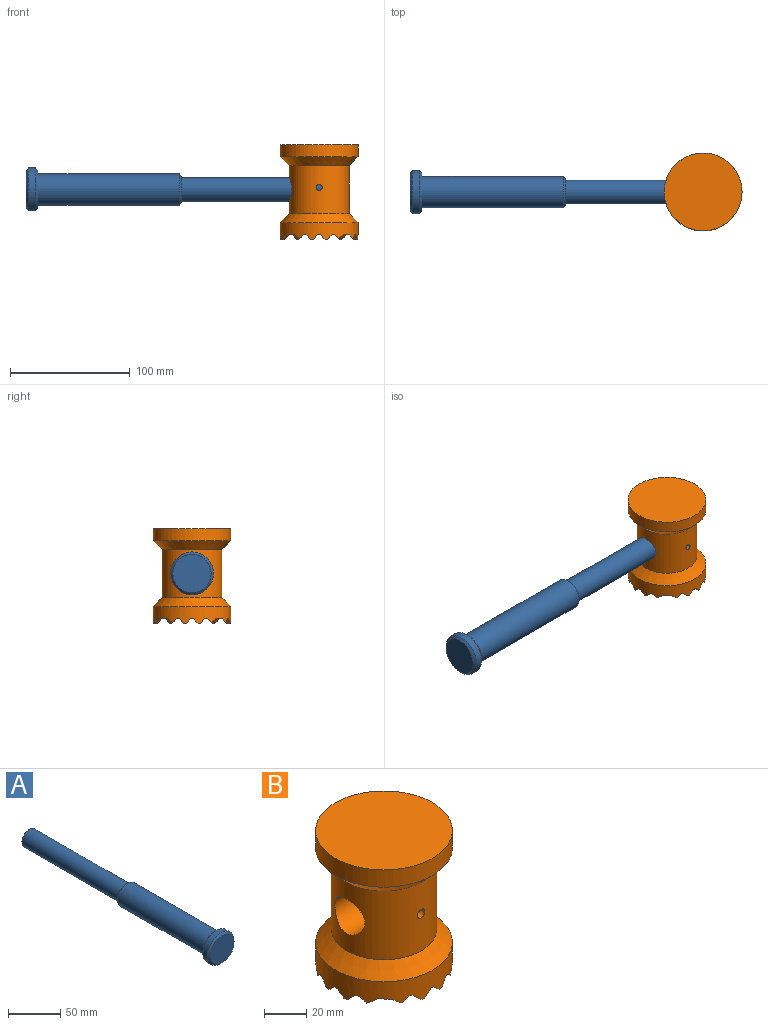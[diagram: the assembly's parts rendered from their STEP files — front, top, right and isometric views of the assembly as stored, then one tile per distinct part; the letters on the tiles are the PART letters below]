
ASSEMBLY  parts=2 mates=1
PART A: 10 faces, bbox 36x260x36 mm
  f0: cylinder r=10mm len=130mm, axis (0,1,0), area 8168.1mm2, adj f1,f3
  f1: plane 20x20mm, normal (0,1,0), area 314.2mm2, adj f0
  f2: cylinder r=13mm len=118mm, axis (0,1,0), area 9638.4mm2, adj f6,f9
  f3: plane 22x22mm, normal (0,1,0), area 66mm2, adj f0,f9
  f4: cylinder r=18mm len=36mm, axis (0,1,0), area 678.6mm2, adj f7,f8
  f5: plane 32x32mm, normal (0,-1,0), area 804.2mm2, adj f8
  f6: plane 32x32mm, normal (0,1,0), area 273.3mm2, adj f2,f7
  f7: cone r=18mm half-angle=45deg, axis (0,-1,0), area 302.1mm2, adj f4,f6
  f8: cone r=16mm half-angle=45deg, axis (0,1,0), area 302.1mm2, adj f4,f5
  f9: cone r=13mm half-angle=45deg, axis (0,-1,0), area 213.3mm2, adj f2,f3
PART B: 137 faces, bbox 65x65x79 mm
  f0: cylinder r=25mm len=50mm, axis (0,0,1), area 5923.4mm2, adj f1,f29,f30,f135,f136
  f1: cylinder r=10mm len=40mm, axis (1,0,0), area 2408.1mm2, adj f0,f134,f135,f136
  f2: plane 2x2mm, normal (0,0,-1), area 4mm2, adj f25,f49,f125,f126
  f3: plane 2x2mm, normal (0,0,-1), area 4mm2, adj f25,f49,f105,f124
  f4: plane 2x2mm, normal (0,0,-1), area 4mm2, adj f25,f49,f99,f104
  f5: plane 2x2mm, normal (0,0,-1), area 4mm2, adj f25,f49,f83,f98
  f6: plane 3.01x2mm, normal (0,0,-1), area 5.7mm2, adj f22,f50,f51,f131
  f7: plane 2x2mm, normal (0,0,-1), area 4mm2, adj f50,f51,f123,f130
  f8: plane 2x2mm, normal (0,0,-1), area 4mm2, adj f50,f51,f107,f122
  f9: plane 2x2mm, normal (0,0,-1), area 4mm2, adj f50,f51,f97,f106
  f10: plane 2x2mm, normal (0,0,-1), area 4mm2, adj f50,f51,f85,f96
  f11: plane 3.01x2mm, normal (0,0,-1), area 5.7mm2, adj f22,f52,f53,f132
  f12: plane 2x2mm, normal (0,0,-1), area 4mm2, adj f52,f53,f119,f129
  f13: plane 2x2mm, normal (0,0,-1), area 4mm2, adj f52,f53,f109,f118
  f14: plane 2x2mm, normal (0,0,-1), area 4mm2, adj f52,f53,f95,f108
  f15: plane 2x2mm, normal (0,0,-1), area 4mm2, adj f52,f53,f87,f94
  f16: plane 2x2mm, normal (0,0,-1), area 4mm2, adj f26,f54,f117,f128
  f17: plane 2x2mm, normal (0,0,-1), area 4mm2, adj f26,f54,f111,f116
  f18: plane 2x2mm, normal (0,0,-1), area 4mm2, adj f26,f54,f93,f110
  f19: plane 2x2mm, normal (0,0,-1), area 4mm2, adj f26,f54,f89,f92
  f20: plane 3.1x2mm, normal (0,0,-1), area 5.8mm2, adj f22,f55,f113,f114
  f21: plane 3.13x2mm, normal (0,0,-1), area 5.9mm2, adj f22,f55,f91,f112
  f22: cylinder r=32.5mm len=65mm, axis (0,0,1), area 2364.1mm2, adj f6,f11,f20,f21,f23,f24,f25,f26
  f23: plane 3.1x2mm, normal (0,0,-1), area 5.8mm2, adj f22,f48,f103,f120
  f24: plane 3.13x2mm, normal (0,0,-1), area 5.9mm2, adj f22,f48,f101,f102
  f25: plane 46.43x4mm, normal (-0.71,0,-0.71), area 138.4mm2, adj f2,f3,f4,f5,f22,f45,f74,f75
  f26: plane 46.43x4mm, normal (0.71,0,-0.71), area 138.4mm2, adj f16,f17,f18,f19,f22,f35,f59,f60
  f27: plane 3.21x2mm, normal (0,0,-1), area 6.1mm2, adj f22,f50,f51,f84
  f28: plane 3.21x2mm, normal (0,0,-1), area 6.1mm2, adj f22,f52,f53,f86
  f29: cone r=25mm half-angle=45deg, axis (0,0,-1), area 1916mm2, adj f0,f22
  f30: cone r=32.5mm half-angle=45deg, axis (0,0,1), area 1916mm2, adj f0,f31
  f31: cylinder r=32.5mm len=65mm, axis (0,0,1), area 2042mm2, adj f30,f32
  f32: plane 65x65mm, normal (0,0,1), area 3318.3mm2, adj f31
  f33: plane 41.53x0.01mm, normal (-1,0,0), area 0.6mm2, adj f22,f34,f55
  f34: plane 45.92x2mm, normal (0,0,-1), area 87.6mm2, adj f22,f33,f35
  f35: plane 45.92x0.01mm, normal (1,0,0), area 0.7mm2, adj f22,f26,f34
  f36: plane 59.57x0.01mm, normal (-1,0,0), area 0.9mm2, adj f22,f37,f54
  f37: plane 61.16x2mm, normal (0,0,-1), area 120.8mm2, adj f22,f36,f38
  f38: plane 61.16x0.01mm, normal (1,0,0), area 0.9mm2, adj f22,f37,f53
  f39: plane 64.97x0.01mm, normal (-1,0,0), area 1mm2, adj f22,f40,f52
  f40: plane 65x2mm, normal (0,0,-1), area 130mm2, adj f22,f39,f41
  f41: plane 64.97x0.01mm, normal (1,0,0), area 1mm2, adj f22,f40,f51
  f42: plane 61.16x0.01mm, normal (-1,0,0), area 0.9mm2, adj f22,f43,f50
  f43: plane 61.16x2mm, normal (0,0,-1), area 120.8mm2, adj f22,f42,f44
  f44: plane 59.57x0.01mm, normal (1,0,0), area 0.9mm2, adj f22,f43,f49
  f45: plane 45.92x0.01mm, normal (-1,0,0), area 0.7mm2, adj f22,f25,f46
  f46: plane 45.92x2mm, normal (0,0,-1), area 87.6mm2, adj f22,f45,f47
  f47: plane 41.53x0.01mm, normal (1,0,0), area 0.6mm2, adj f22,f46,f48
  f48: plane 41.53x4mm, normal (0.71,0,-0.71), area 106.6mm2, adj f22,f23,f24,f47,f79,f80,f81,f100
  f49: plane 59.57x4mm, normal (0.71,0,-0.71), area 161.7mm2, adj f2,f3,f4,f5,f22,f44,f74,f75
  f50: plane 63.47x4mm, normal (-0.71,0,-0.71), area 187.4mm2, adj f6,f7,f8,f9,f10,f22,f27,f42
  f51: plane 64.98x4.01mm, normal (0.71,0,-0.71), area 200.3mm2, adj f6,f7,f8,f9,f10,f22,f27,f41
  f52: plane 64.98x4.01mm, normal (-0.71,0,-0.71), area 200.3mm2, adj f11,f12,f13,f14,f15,f22,f28,f39
  f53: plane 63.47x4mm, normal (0.71,0,-0.71), area 187.4mm2, adj f11,f12,f13,f14,f15,f22,f28,f38
  f54: plane 59.57x4mm, normal (-0.71,0,-0.71), area 161.7mm2, adj f16,f17,f18,f19,f22,f36,f59,f60
  f55: plane 41.53x4mm, normal (-0.71,0,-0.71), area 106.6mm2, adj f20,f21,f22,f33,f56,f57,f58,f90
  f56: plane 5.45x2.51mm, normal (0,0,-1), area 12.5mm2, adj f22,f55,f90,f91
  f57: plane 7.24x2.51mm, normal (0,0,-1), area 18.2mm2, adj f22,f55,f112,f113
  f58: plane 5.38x2.51mm, normal (0,0,-1), area 12.3mm2, adj f22,f55,f114,f115
  f59: plane 9.49x2.51mm, normal (0,0,-1), area 21.8mm2, adj f22,f26,f54,f88,f89
  f60: plane 9.49x2.51mm, normal (0,0,-1), area 23.8mm2, adj f26,f54,f92,f93
  f61: plane 9.49x2.51mm, normal (0,0,-1), area 23.8mm2, adj f26,f54,f110,f111
  f62: plane 9.49x2.51mm, normal (0,0,-1), area 23.8mm2, adj f26,f54,f116,f117
  f63: plane 9.49x2.51mm, normal (0,0,-1), area 21.3mm2, adj f22,f26,f54,f128,f133
  f64: plane 9.49x2.51mm, normal (0,0,-1), area 23.8mm2, adj f52,f53,f86,f87
  f65: plane 9.49x2.51mm, normal (0,0,-1), area 23.8mm2, adj f52,f53,f94,f95
  f66: plane 9.49x2.51mm, normal (0,0,-1), area 23.8mm2, adj f52,f53,f108,f109
  f67: plane 9.49x2.51mm, normal (0,0,-1), area 23.8mm2, adj f52,f53,f118,f119
  f68: plane 9.49x2.51mm, normal (0,0,-1), area 23.8mm2, adj f52,f53,f129,f132
  f69: plane 9.49x2.51mm, normal (0,0,-1), area 23.8mm2, adj f50,f51,f84,f85
  f70: plane 9.49x2.51mm, normal (0,0,-1), area 23.8mm2, adj f50,f51,f96,f97
  f71: plane 9.49x2.51mm, normal (0,0,-1), area 23.8mm2, adj f50,f51,f106,f107
  f72: plane 9.49x2.51mm, normal (0,0,-1), area 23.8mm2, adj f50,f51,f122,f123
  f73: plane 9.49x2.51mm, normal (0,0,-1), area 23.8mm2, adj f50,f51,f130,f131
  f74: plane 9.49x2.51mm, normal (0,0,-1), area 21.8mm2, adj f22,f25,f49,f82,f83
  f75: plane 9.49x2.51mm, normal (0,0,-1), area 23.8mm2, adj f25,f49,f98,f99
  f76: plane 9.49x2.51mm, normal (0,0,-1), area 23.8mm2, adj f25,f49,f104,f105
  f77: plane 9.49x2.51mm, normal (0,0,-1), area 23.8mm2, adj f25,f49,f124,f125
  f78: plane 9.49x2.51mm, normal (0,0,-1), area 21.3mm2, adj f22,f25,f49,f126,f127
  f79: plane 5.45x2.51mm, normal (0,0,-1), area 12.5mm2, adj f22,f48,f100,f101
  f80: plane 7.24x2.51mm, normal (0,0,-1), area 18.2mm2, adj f22,f48,f102,f103
  f81: plane 5.38x2.51mm, normal (0,0,-1), area 12.3mm2, adj f22,f48,f120,f121
  f82: plane 7.32x2.99mm, normal (0,-0.71,-0.71), area 16mm2, adj f22,f49,f74
  f83: plane 9.49x3.74mm, normal (0,0.71,-0.71), area 30.4mm2, adj f5,f25,f49,f74
  f84: plane 9.49x3.74mm, normal (0,-0.71,-0.71), area 30.4mm2, adj f27,f50,f51,f69
  f85: plane 9.49x3.74mm, normal (0,0.71,-0.71), area 30.4mm2, adj f10,f50,f51,f69
  f86: plane 9.49x3.74mm, normal (0,-0.71,-0.71), area 30.4mm2, adj f28,f52,f53,f64
  f87: plane 9.49x3.74mm, normal (0,0.71,-0.71), area 30.4mm2, adj f15,f52,f53,f64
  f88: plane 7.32x2.99mm, normal (0,-0.71,-0.71), area 16mm2, adj f22,f54,f59
  f89: plane 9.49x3.74mm, normal (0,0.71,-0.71), area 30.4mm2, adj f19,f26,f54,f59
  f90: plane 4.46x2.96mm, normal (0,-0.71,-0.71), area 9.5mm2, adj f22,f55,f56
  f91: plane 6.5x3.74mm, normal (0,0.71,-0.71), area 21.9mm2, adj f21,f22,f55,f56
  f92: plane 9.49x3.74mm, normal (0,-0.71,-0.71), area 30.4mm2, adj f19,f26,f54,f60
  f93: plane 9.49x3.74mm, normal (0,0.71,-0.71), area 30.4mm2, adj f18,f26,f54,f60
  f94: plane 9.49x3.74mm, normal (0,-0.71,-0.71), area 30.4mm2, adj f15,f52,f53,f65
  f95: plane 9.49x3.74mm, normal (0,0.71,-0.71), area 30.4mm2, adj f14,f52,f53,f65
  f96: plane 9.49x3.74mm, normal (0,-0.71,-0.71), area 30.4mm2, adj f10,f50,f51,f70
  f97: plane 9.49x3.74mm, normal (0,0.71,-0.71), area 30.4mm2, adj f9,f50,f51,f70
  f98: plane 9.49x3.74mm, normal (0,-0.71,-0.71), area 30.4mm2, adj f5,f25,f49,f75
  f99: plane 9.49x3.74mm, normal (0,0.71,-0.71), area 30.4mm2, adj f4,f25,f49,f75
  f100: plane 4.46x2.96mm, normal (0,-0.71,-0.71), area 9.5mm2, adj f22,f48,f79
  f101: plane 6.5x3.74mm, normal (0,0.71,-0.71), area 21.9mm2, adj f22,f24,f48,f79
  f102: plane 7.23x3.75mm, normal (0,-0.71,-0.71), area 27.6mm2, adj f22,f24,f48,f80
  f103: plane 7.23x3.75mm, normal (0,0.71,-0.71), area 27.5mm2, adj f22,f23,f48,f80
  f104: plane 9.49x3.74mm, normal (0,-0.71,-0.71), area 30.4mm2, adj f4,f25,f49,f76
  f105: plane 9.49x3.74mm, normal (0,0.71,-0.71), area 30.4mm2, adj f3,f25,f49,f76
  f106: plane 9.49x3.74mm, normal (0,-0.71,-0.71), area 30.4mm2, adj f9,f50,f51,f71
  f107: plane 9.49x3.74mm, normal (0,0.71,-0.71), area 30.4mm2, adj f8,f50,f51,f71
  f108: plane 9.49x3.74mm, normal (0,-0.71,-0.71), area 30.4mm2, adj f14,f52,f53,f66
  f109: plane 9.49x3.74mm, normal (0,0.71,-0.71), area 30.4mm2, adj f13,f52,f53,f66
  f110: plane 9.49x3.74mm, normal (0,-0.71,-0.71), area 30.4mm2, adj f18,f26,f54,f61
  f111: plane 9.49x3.74mm, normal (0,0.71,-0.71), area 30.4mm2, adj f17,f26,f54,f61
  f112: plane 7.23x3.75mm, normal (0,-0.71,-0.71), area 27.6mm2, adj f21,f22,f55,f57
  f113: plane 7.23x3.75mm, normal (0,0.71,-0.71), area 27.5mm2, adj f20,f22,f55,f57
  f114: plane 6.46x3.74mm, normal (0,-0.71,-0.71), area 21.6mm2, adj f20,f22,f55,f58
  f115: plane 4.37x2.89mm, normal (0,0.71,-0.71), area 9.1mm2, adj f22,f55,f58
  f116: plane 9.49x3.74mm, normal (0,-0.71,-0.71), area 30.4mm2, adj f17,f26,f54,f62
  f117: plane 9.49x3.74mm, normal (0,0.71,-0.71), area 30.4mm2, adj f16,f26,f54,f62
  f118: plane 9.49x3.74mm, normal (0,-0.71,-0.71), area 30.4mm2, adj f13,f52,f53,f67
  f119: plane 9.49x3.74mm, normal (0,0.71,-0.71), area 30.4mm2, adj f12,f52,f53,f67
  f120: plane 6.46x3.74mm, normal (0,-0.71,-0.71), area 21.6mm2, adj f22,f23,f48,f81
  f121: plane 4.37x2.89mm, normal (0,0.71,-0.71), area 9.1mm2, adj f22,f48,f81
  f122: plane 9.49x3.74mm, normal (0,-0.71,-0.71), area 30.4mm2, adj f8,f50,f51,f72
  f123: plane 9.49x3.74mm, normal (0,0.71,-0.71), area 30.4mm2, adj f7,f50,f51,f72
  f124: plane 9.49x3.74mm, normal (0,-0.71,-0.71), area 30.4mm2, adj f3,f25,f49,f77
  f125: plane 9.49x3.74mm, normal (0,0.71,-0.71), area 30.4mm2, adj f2,f25,f49,f77
  f126: plane 9.49x3.74mm, normal (0,-0.71,-0.71), area 30.4mm2, adj f2,f25,f49,f78
  f127: plane 7.07x2.86mm, normal (0,0.71,-0.71), area 14.8mm2, adj f22,f49,f78
  f128: plane 9.49x3.74mm, normal (0,-0.71,-0.71), area 30.4mm2, adj f16,f26,f54,f63
  f129: plane 9.49x3.74mm, normal (0,-0.71,-0.71), area 30.4mm2, adj f12,f52,f53,f68
  f130: plane 9.49x3.74mm, normal (0,-0.71,-0.71), area 30.4mm2, adj f7,f50,f51,f73
  f131: plane 9.49x3.74mm, normal (0,0.71,-0.71), area 30.4mm2, adj f6,f50,f51,f73
  f132: plane 9.49x3.74mm, normal (0,0.71,-0.71), area 30.4mm2, adj f11,f52,f53,f68
  f133: plane 7.07x2.86mm, normal (0,0.71,-0.71), area 14.8mm2, adj f22,f54,f63
  f134: plane 20x20mm, normal (-1,0,0), area 314.2mm2, adj f1
  f135: cylinder r=2.5mm len=15.87mm, axis (0,1,0), area 239.2mm2, adj f0,f1
  f136: cylinder r=2.5mm len=15.87mm, axis (0,1,0), area 239.2mm2, adj f0,f1
PLACE A rot(axis=(-0.58,-0.58,-0.58),120deg) t=(12.39,3.72,9.96)mm
PLACE B t=(-2.61,3.72,-2.61)mm fixed
MATE planar A.f0 <-> B.f1  axis (1,0,0) through (12.39,3.72,9.96)mm
